# Revit family: AWN4
name_source: partatom
category: Lighting Fixtures
revit_build: Autodesk Revit Architecture 2012 (Build: 20110309_2315(x64)
units: mm (PartAtom-declared; Revit-internal decimal feet)

## types (1)
- AWN4-232
    Apparent Load = 0 VA
    Backbox = White
    Ballast = Electronic T8, Instant Start
    Color Filter = 16777215
    Default Elevation = 48.000"
    Description = The AW is a low profile wraparound fixture that offers two, three, or four lamp cross sections.
    Dimming Lamp Color Temperature Shift = <None>
    Emit from Line Length = 45.000"
    Glass = Glass
    Lamp = F32T8
    Lamp Type = 4', T8: 32, 30, 28 or 25 Watt
    Manufacturer = Columbia Lighting
    Manufacturer Fax = 866-898-1065
    Model = AWN
    Photometric Web File = 12409.IES
    Product Documentation Link = http://www.columbialighting.com
    Product Page URL = http://www.columbialighting.com
    Tilt Angle = 90.00°
    URL = http://www.columbialighting.com
    Voltage = 0 V
    Wattage Comments = 54 W

## geometry (parser evidence)
native form markers: Sweep x1
no freeform markers — native parametric forms only
